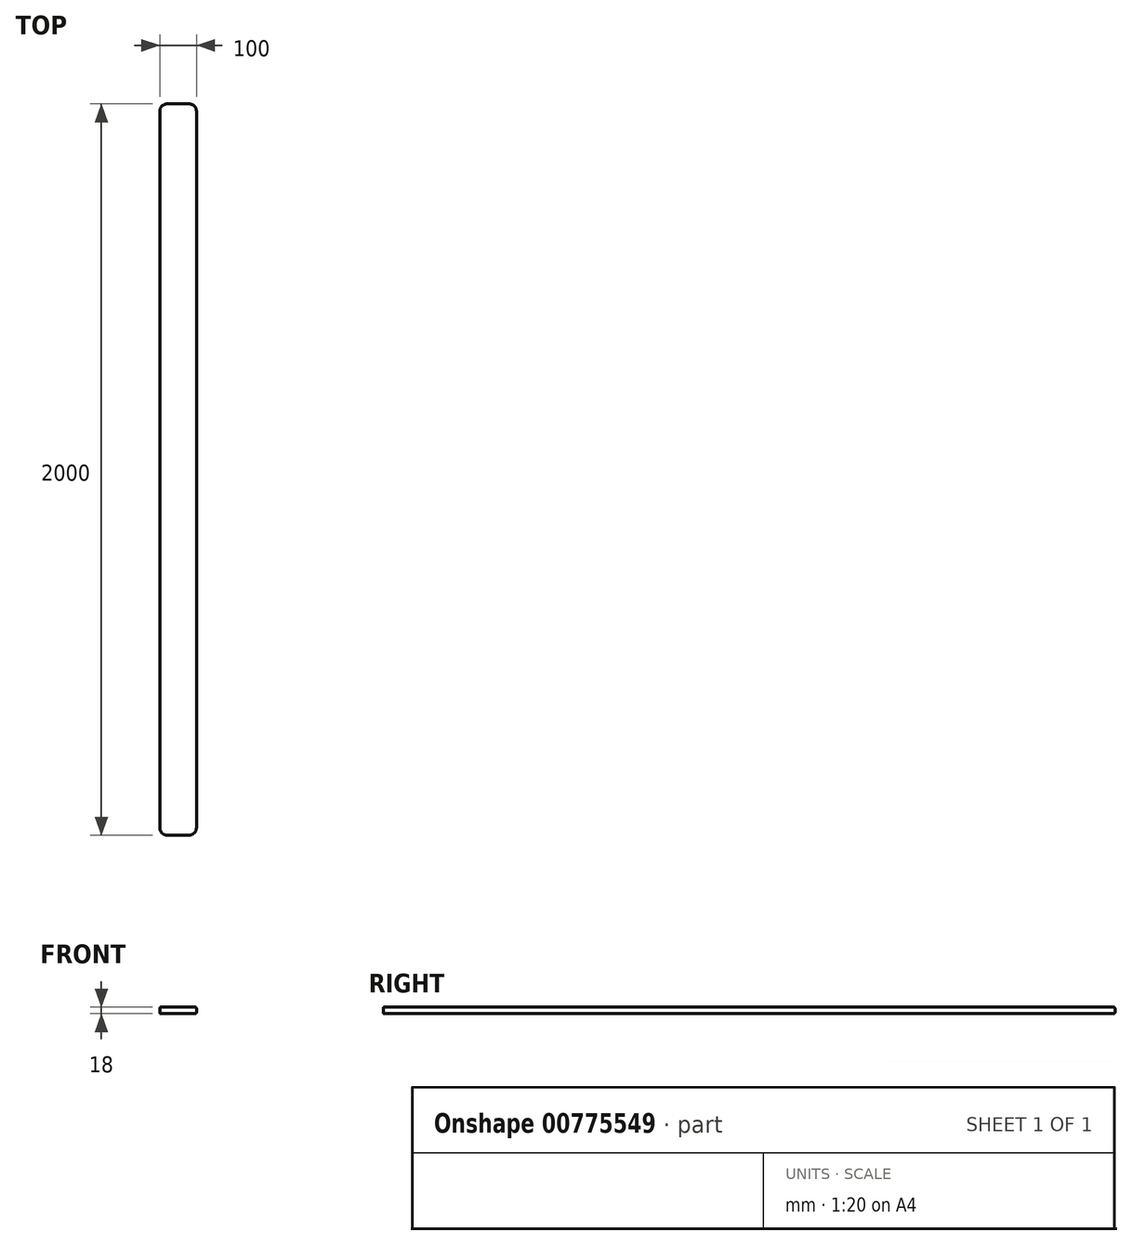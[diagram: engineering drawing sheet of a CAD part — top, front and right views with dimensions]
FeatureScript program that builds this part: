
annotation { "Feature Type Name" : "Feature", "Feature Type Description" : "" }
export const myFeature = defineFeature(function(context is Context, id is Id, definition is map)
    precondition{}
    {
        {
            var Q0;
            Q0=qCreatedBy(makeId("Front.planeOp"),FACE);
            var sketch = newSketch(context, id + "F0", { "sketchPlane" : qUnion([Q0])});
            skLineSegment(sketch, "E0.bottom", {"start": v(0, 0) * mm, "end": v(100, 0) * mm});
            skLineSegment(sketch, "E0.top", {"start": v(0, 18) * mm, "end": v(100, 18) * mm});
            skLineSegment(sketch, "E0.left", {"start": v(0, 0) * mm, "end": v(0, 18) * mm});
            skLineSegment(sketch, "E0.right", {"start": v(100, 0) * mm, "end": v(100, 18) * mm});
            skSolve(sketch);
        }
        {
            var Q0;
            Q0=makeQuery(id+"F0.imprint","IMPRINT",FACE,{"disambiguationData":[TD([[makeQuery(id+"F0.imprint","IMPRINT",EDGE,{"derivedFrom":sQuery(id+"F0.wireOp",EDGE,"E0.bottom")}),1.0]])]});
            extrude(context, id + "F1", {"entities" : qUnion([Q0]), "depth" : 2000 * mm, "offsetDistance" : 25 * mm});
        }
        {
            var Q0;
            Q0=makeQuery(id+"F1.opExtrude","SWEPT_FACE",FACE,{"disambiguationData":[OSD([sQuery(id+"F0.wireOp",EDGE,"E0.top")])]});
            var sketch = newSketch(context, id + "F2", { "sketchPlane" : qUnion([Q0])});
            skLineSegment(sketch, "E1", {"start": v(50, 0) * mm, "end": v(50, -50) * mm, "construction": true});
            skLineSegment(sketch, "E2", {"start": v(50, -50) * mm, "end": v(0, -50) * mm, "construction": true});
            skSolve(sketch);
        }
        {
            var Q0;
            Q0=makeQuery(id+"F1.opExtrude","CAP_EDGE",EDGE,{"disambiguationData":[OSD([sQuery(id+"F0.wireOp",EDGE,"E0.right")])],"isStart":true});
            var Q1;
            Q1=makeQuery(id+"F1.opExtrude","CAP_EDGE",EDGE,{"disambiguationData":[OSD([sQuery(id+"F0.wireOp",EDGE,"E0.left")])],"isStart":true});
            fillet(context, id + "F3", {"entities" : qUnion([Q0, Q1]), "radius" : 20 * mm, "tangentPropagation" : true, "allowEdgeOverflow" : false});
        }
        {
            var Q0;
            Q0=makeQuery(id+"F1.opExtrude","CAP_EDGE",EDGE,{"disambiguationData":[OSD([sQuery(id+"F0.wireOp",EDGE,"E0.right")])],"isStart":false});
            var Q1;
            Q1=makeQuery(id+"F1.opExtrude","CAP_EDGE",EDGE,{"disambiguationData":[OSD([sQuery(id+"F0.wireOp",EDGE,"E0.left")])],"isStart":false});
            fillet(context, id + "F4", {"entities" : qUnion([Q0, Q1]), "radius" : 20 * mm, "tangentPropagation" : true, "allowEdgeOverflow" : false});
        }
        {
            var Q0;
            Q0=makeQuery(id+"F1.opExtrude","SWEPT_EDGE",EDGE,{"disambiguationData":[OSD([sQuery(id+"F0.wireOp",EDGE,"E0.top"),sQuery(id+"F0.wireOp",EDGE,"E0.right")])]});
            var Q1;
            Q1=makeQuery(id+"F1.opExtrude","SWEPT_FACE",FACE,{"disambiguationData":[OSD([sQuery(id+"F0.wireOp",EDGE,"E0.bottom")])]});
            fillet(context, id + "F5", {"entities" : qUnion([Q0, Q1]), "radius" : 3 * mm, "tangentPropagation" : true, "allowEdgeOverflow" : false});
        }
    });
